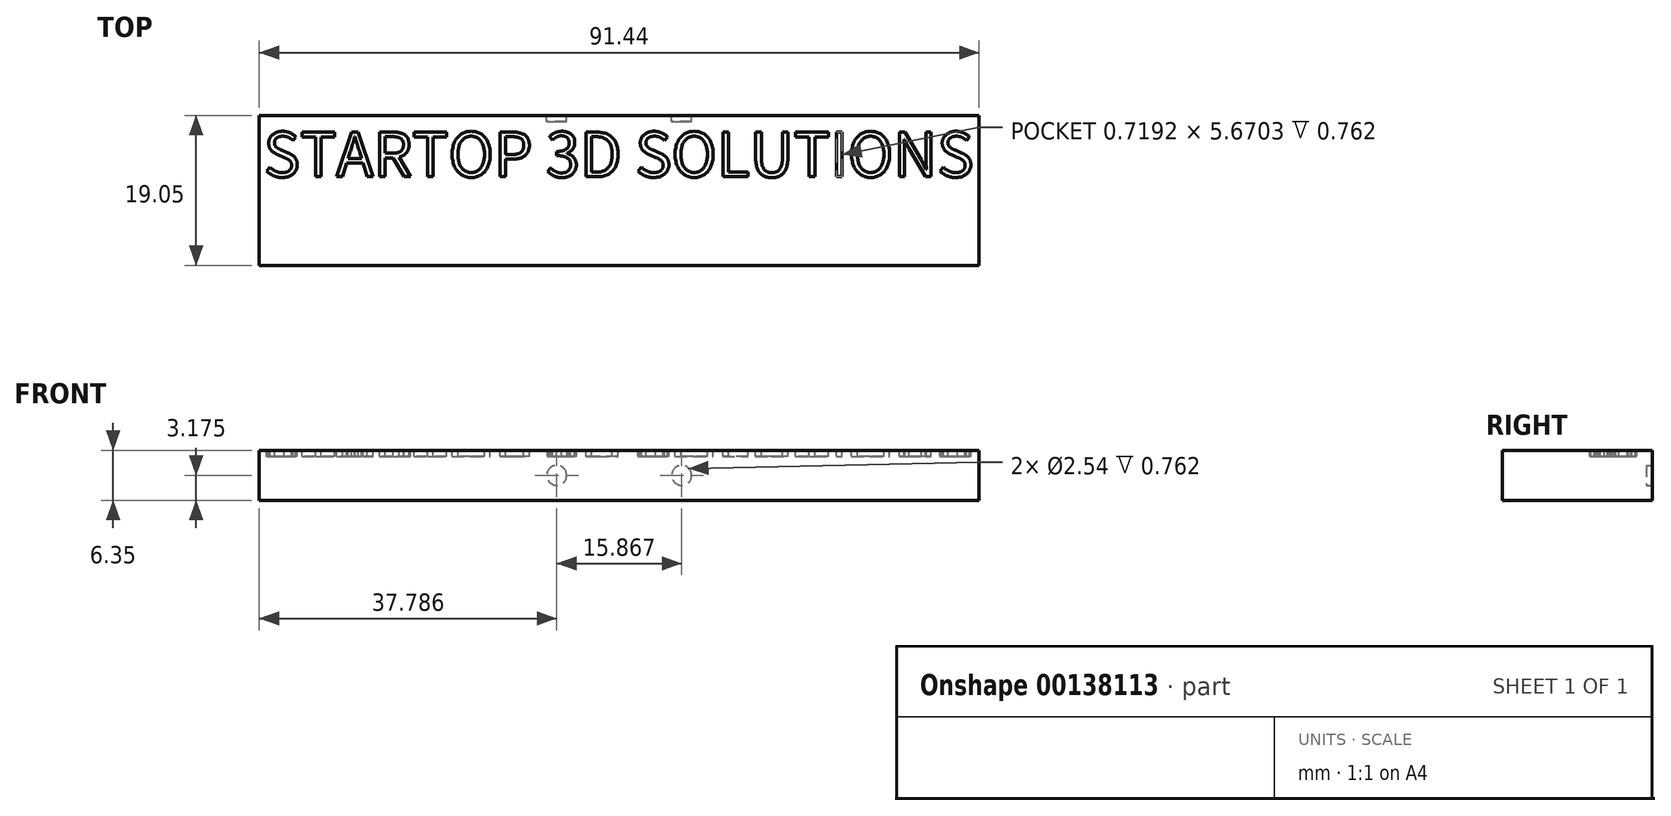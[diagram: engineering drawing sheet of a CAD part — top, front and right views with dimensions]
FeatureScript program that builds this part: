
annotation { "Feature Type Name" : "Feature", "Feature Type Description" : "" }
export const myFeature = defineFeature(function(context is Context, id is Id, definition is map)
    precondition{}
    {
        {
            var Q0;
            Q0=qCreatedBy(makeId("Top.planeOp"),FACE);
            var sketch = newSketch(context, id + "F0", { "sketchPlane" : qUnion([Q0])});
            skLineSegment(sketch, "E0.bottom", {"start": v(0, 0) * mm, "end": v(91.44, 0) * mm});
            skLineSegment(sketch, "E0.top", {"start": v(0, 19.05) * mm, "end": v(91.44, 19.05) * mm});
            skLineSegment(sketch, "E0.left", {"start": v(0, 0) * mm, "end": v(0, 19.05) * mm});
            skLineSegment(sketch, "E0.right", {"start": v(91.44, 0) * mm, "end": v(91.44, 19.05) * mm});
            skSolve(sketch);
        }
        {
            var Q0;
            Q0=qSketchRegion(id+"F0",true);
            extrude(context, id + "F1", {"entities" : qUnion([Q0]), "depth" : 6.35 * mm});
        }
        {
            var Q0;
            Q0=makeQuery(id+"F1.opExtrude","CAP_FACE",FACE,{"disambiguationData":[OSD([sQuery(id+"F0.wireOp",EDGE,"E0.bottom"),sQuery(id+"F0.wireOp",EDGE,"E0.top"),sQuery(id+"F0.wireOp",EDGE,"E0.left"),sQuery(id+"F0.wireOp",EDGE,"E0.right")])],"isStart":false});
            var sketch = newSketch(context, id + "F2", { "sketchPlane" : qUnion([Q0])});
            skLineSegment(sketch, "E1", {"start": v(0, 9.53) * mm, "end": v(91.44, 9.53) * mm, "construction": true});
            skText(sketch, "E2", { "text": "STARTOP 3D SOLUTIONS", "fontName": "NotoSansCJKsc-Regular.otf"});
            const initialGuessF2  = {"E2": [0.00056, 0.01126, 1, 0, 0.00557]};
            skSetInitialGuess(sketch, initialGuessF2);
            skSolve(sketch);
        }
        {
            var Q0;
            Q0=qSketchRegion(id+"F2",true);
            extrude(context, id + "F3", {"entities" : qUnion([Q0]), "operationType" : NewBodyOperationType.REMOVE, "oppositeDirection" : true, "depth" : 0.76 * mm});
        }
        {
            var Q0;
            Q0=makeQuery(id+"F1.opExtrude","SWEPT_FACE",FACE,{"disambiguationData":[OSD([sQuery(id+"F0.wireOp",EDGE,"E0.top")])]});
            var sketch = newSketch(context, id + "F4", { "sketchPlane" : qUnion([Q0])});
            skLineSegment(sketch, "E3", {"start": v(-91.44, 3.18) * mm, "end": v(0, 3.18) * mm, "construction": true});
            skLineSegment(sketch, "E4", {"start": v(-45.72, 6.35) * mm, "end": v(-45.72, 0) * mm, "construction": true});
            skCircle(sketch, "E5", {"center": v(-53.65, 3.18) * mm, "radius": 1.27 * mm});
            skCircle(sketch, "E6.MirrorC", {"center": v(-37.79, 3.18) * mm, "radius": 1.27 * mm});
            skSolve(sketch);
        }
        {
            var Q0;
            Q0 = qSketchRegion(id + "F4", true);
            extrude(context, id + "F5", {"entities" : qUnion([Q0]), "operationType" : NewBodyOperationType.REMOVE, "oppositeDirection" : true, "depth" : 0.76 * mm});
        }
    });
